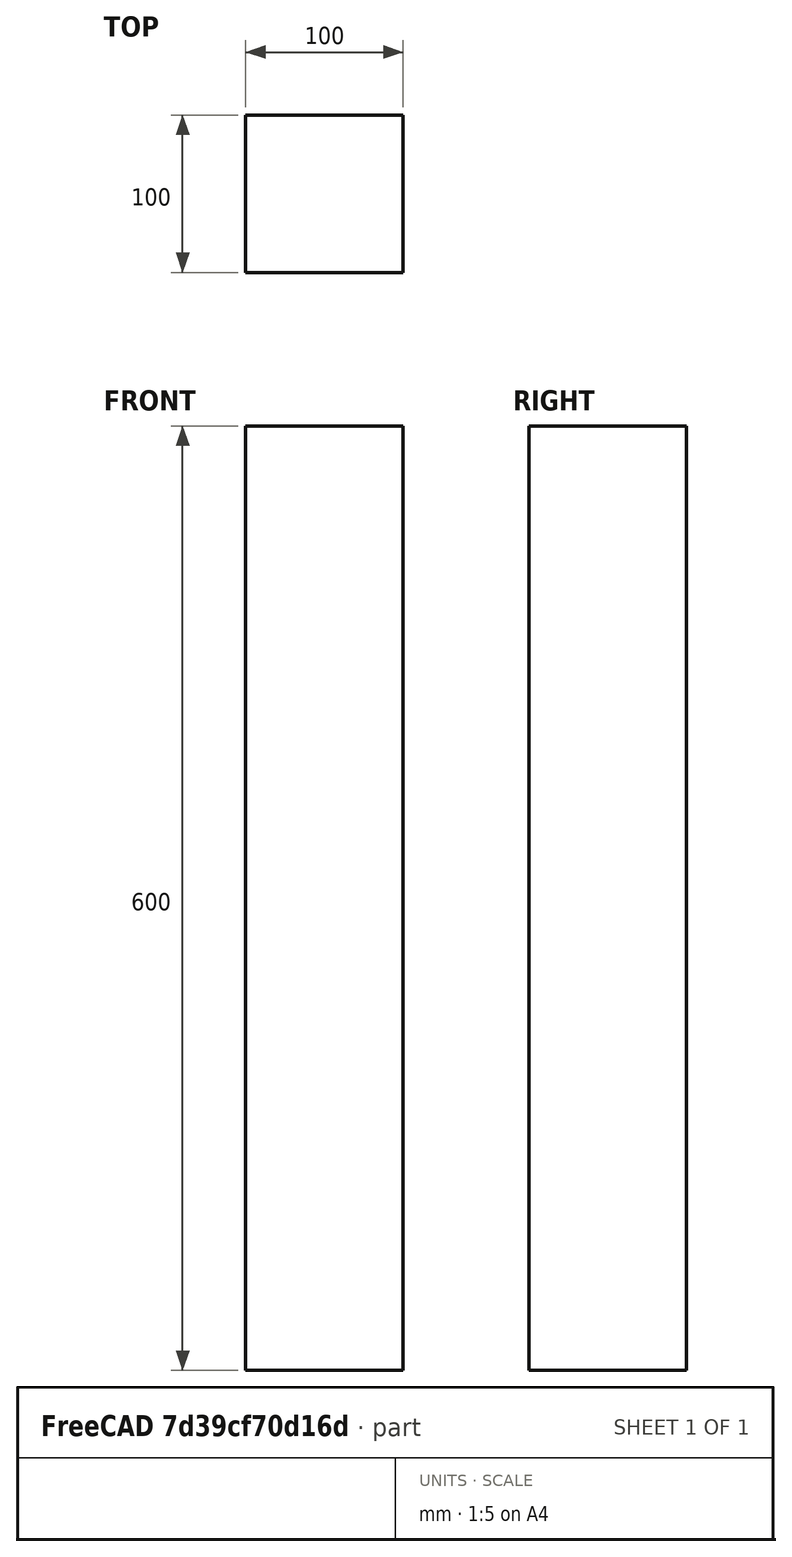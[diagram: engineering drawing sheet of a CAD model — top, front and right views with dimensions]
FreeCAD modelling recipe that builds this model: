
FCSTD DOCUMENT  (FreeCAD 1.0R39109 (Git))
Label: 045_table_bottom_frame_small
License: All rights reserved
LicenseURL: http://en.wikipedia.org/wiki/All_rights_reserved
objects: Sketcher::SketchObject×1, Spreadsheet::Sheet×1, PartDesign::Pad×1, PartDesign::Body×1
note: 6 computed .brp shape members not serialized (recipe doc carries the construction recipe); baked Part::Feature solids carry a one-line shape summary decoded from their .brp

FEATURE [Sketcher::SketchObject] Sketch
  ArcFitTolerance = 1e-06
  AttachmentSupport = -> [XY_Plane]
  FullyConstrained = true
  MakeInternals = false
  MapMode = 5
  expr: Constraints[11] = Spreadsheet.width
  expr: Constraints[12] = Spreadsheet.length
  sketch-geometry (5):
    g0: LineSegment StartX=-50 StartY=50 StartZ=0 EndX=-50 EndY=-50 EndZ=0
    g1: LineSegment StartX=-50 StartY=-50 StartZ=0 EndX=50 EndY=-50 EndZ=0
    g2: LineSegment StartX=50 StartY=-50 StartZ=0 EndX=50 EndY=50 EndZ=0
    g3: LineSegment StartX=50 StartY=50 StartZ=0 EndX=-50 EndY=50 EndZ=0
    g4: LineSegment [constr] StartX=-50 StartY=50 StartZ=0 EndX=50 EndY=-50 EndZ=0
  constraints (13):
    c: Coincident(g0,g1)
    c: Coincident(g1,g2)
    c: Coincident(g2,g3)
    c: Coincident(g3,g0)
    c: Vertical(g0)
    c: Vertical(g2)
    c: Horizontal(g1)
    c: Horizontal(g3)
    c: Coincident(g4,g0)
    c: Coincident(g4,g1)
    c: Symmetric(g4,g4,g-1)
    c: Distance(g0,g0) = 100
    c: Distance(g3,g3) = 100
FEATURE [Spreadsheet::Sheet] Spreadsheet
  cells = A2='length; B2(length)=100; A3='width; B3(width)=100; A4='height; B4(height)=600
FEATURE [PartDesign::Pad] Pad
  Direction = (0,0,1)
  Length = 600
  Length2 = 10
  Midplane = true
  Profile = -> Sketch
  ReferenceAxis = -> Sketch [N_Axis]
  Suppressed = false
  Type = 0
  expr: Length = Spreadsheet.height
FEATURE [PartDesign::Body] Body
  AllowCompound = false
  Group = -> [Sketch,Pad]
  Origin = -> Origin
  Tip = -> Pad
